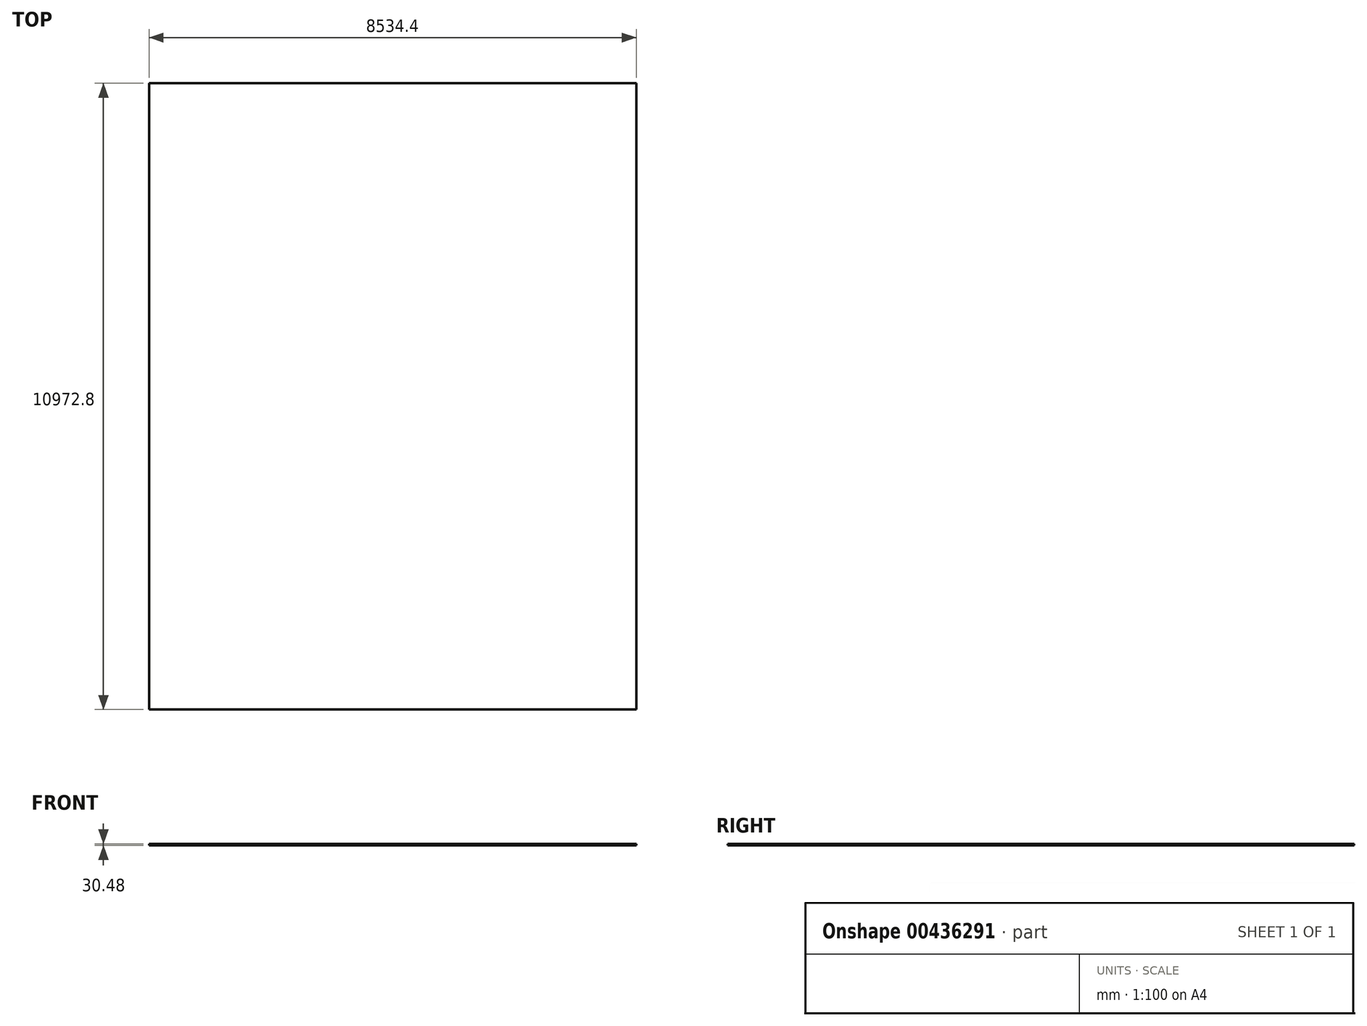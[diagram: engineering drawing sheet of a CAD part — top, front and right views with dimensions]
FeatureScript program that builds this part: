
annotation { "Feature Type Name" : "Feature", "Feature Type Description" : "" }
export const myFeature = defineFeature(function(context is Context, id is Id, definition is map)
    precondition{}
    {
        {
            var Q0;
            Q0=qCreatedBy(makeId("Top.planeOp"),FACE);
            var sketch = newSketch(context, id + "F0", { "sketchPlane" : qUnion([Q0])});
            skLineSegment(sketch, "E0.bottom", {"start": v(-4261.32, 7714.83) * mm, "end": v(4273.08, 7714.83) * mm});
            skLineSegment(sketch, "E0.top", {"start": v(-4261.32, -3257.97) * mm, "end": v(4273.08, -3257.97) * mm});
            skLineSegment(sketch, "E0.left", {"start": v(-4261.32, 7714.83) * mm, "end": v(-4261.32, -3257.97) * mm});
            skLineSegment(sketch, "E0.right", {"start": v(4273.08, 7714.83) * mm, "end": v(4273.08, -3257.97) * mm});
            skSolve(sketch);
        }
        {
            var Q0;
            Q0=makeQuery(id+"F0.imprint","IMPRINT",FACE,{"disambiguationData":[TD([[makeQuery(id+"F0.imprint","IMPRINT",EDGE,{"derivedFrom":sQuery(id+"F0.wireOp",EDGE,"E0.bottom")}),-1.0]])]});
            extrude(context, id + "F1", {"entities" : qUnion([Q0]), "depth" : 30.48 * mm});
        }
    });
